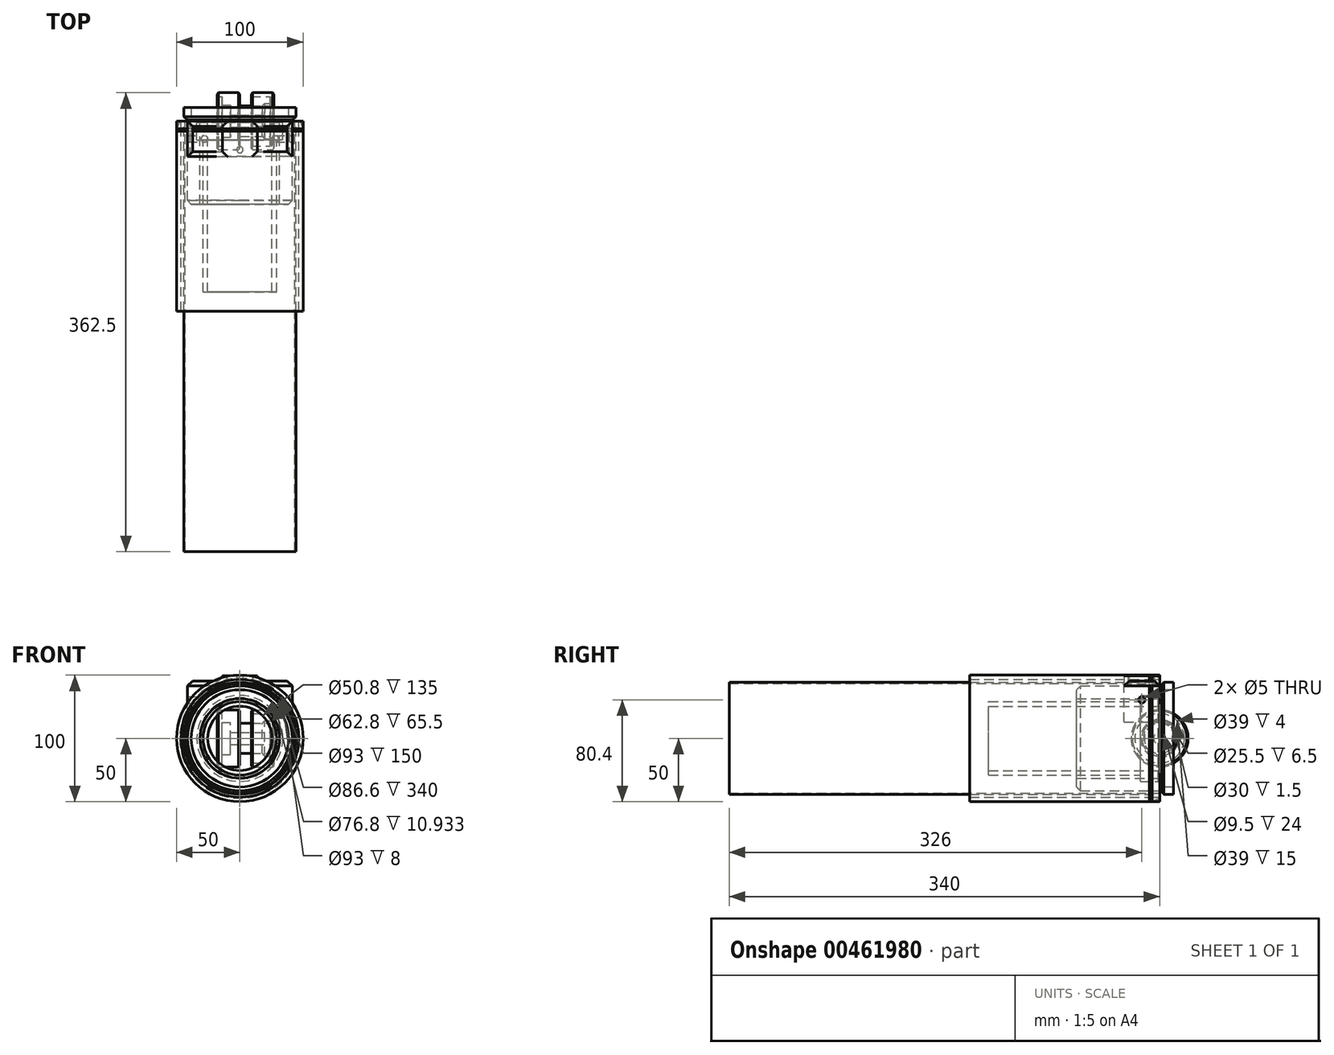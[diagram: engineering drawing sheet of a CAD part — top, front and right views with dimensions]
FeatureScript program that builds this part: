
annotation { "Feature Type Name" : "Feature", "Feature Type Description" : "" }
export const myFeature = defineFeature(function(context is Context, id is Id, definition is map)
    precondition{}
    {
        {
            var Q0;
            Q0=qCreatedBy(makeId("Front.planeOp"),FACE);
            var sketch = newSketch(context, id + "F0", { "sketchPlane" : qUnion([Q0])});
            skCircle(sketch, "E0", {"center": v(0, 0) * mm, "radius": 41.4 * mm});
            skCircle(sketch, "E1", {"center": v(0, 0) * mm, "radius": 31.4 * mm});
            skSolve(sketch);
        }
        {
            var Q0;
            Q0=makeQuery(id+"F0.imprint","IMPRINT",FACE,{"disambiguationData":[TD([[makeQuery(id+"F0.imprint","IMPRINT",EDGE,{"derivedFrom":sQuery(id+"F0.wireOp",EDGE,"E0")}),1.0]])]});
            extrude(context, id + "F1", {"entities" : qUnion([Q0]), "depth" : 65.5 * mm});
        }
        {
            var Q0;
            Q0=makeQuery(id+"F1.opExtrude","CAP_EDGE",EDGE,{"disambiguationData":[OSD([sQuery(id+"F0.wireOp",EDGE,"E0")])],"isStart":false});
            chamfer(context, id + "F2", {"entities" : qUnion([Q0]), "width" : 3 * mm, "tangentPropagation" : true});
        }
        {
            var Q0;
            Q0=qCreatedBy(makeId("Front.planeOp"),FACE);
            var sketch = newSketch(context, id + "F3", { "sketchPlane" : qUnion([Q0])});
            skCircle(sketch, "E2", {"center": v(0, 0) * mm, "radius": 25.4 * mm});
            skCircle(sketch, "E3", {"center": v(0, 0) * mm, "radius": 34 * mm});
            skSolve(sketch);
        }
        {
            var Q0;
            Q0=makeQuery(id+"F3.imprint","IMPRINT",FACE,{"disambiguationData":[TD([[makeQuery(id+"F3.imprint","IMPRINT",EDGE,{"derivedFrom":sQuery(id+"F3.wireOp",EDGE,"E2")}),-1.0]])]});
            extrude(context, id + "F4", {"entities" : qUnion([Q0]), "depth" : 15 * mm});
        }
        {
            var Q0;
            Q0=makeQuery(id+"F4.opExtrude","CAP_FACE",FACE,{"disambiguationData":[OSD([sQuery(id+"F3.wireOp",EDGE,"E2"),sQuery(id+"F3.wireOp",EDGE,"E3")])],"isStart":false});
            var sketch = newSketch(context, id + "F5", { "sketchPlane" : qUnion([Q0])});
            skCircle(sketch, "E4", {"center": v(0, 0) * mm, "radius": 29 * mm});
            skCircle(sketch, "E5", {"center": v(0, 0) * mm, "radius": 25.4 * mm});
            skSolve(sketch);
        }
        {
            var Q0;
            Q0=makeQuery(id+"F5.imprint","IMPRINT",FACE,{"disambiguationData":[TD([[makeQuery(id+"F5.imprint","IMPRINT",EDGE,{"derivedFrom":sQuery(id+"F5.wireOp",EDGE,"E4")}),1.0]])]});
            extrude(context, id + "F6", {"entities" : qUnion([Q0]), "operationType" : NewBodyOperationType.ADD, "depth" : 120 * mm});
        }
        {
            var Q0;
            Q0=makeQuery(id+"F4.opExtrude","CAP_EDGE",EDGE,{"disambiguationData":[OSD([sQuery(id+"F3.wireOp",EDGE,"E3")])],"isStart":true});
            chamfer(context, id + "F7", {"entities" : qUnion([Q0]), "chamferType" : ChamferType.TWO_OFFSETS, "width1" : 1 * mm, "oppositeDirection" : false, "width2" : 2 * mm, "tangentPropagation" : true});
        }
        {
            var Q0;
            Q0=qCreatedBy(makeId("Right.planeOp"),FACE);
            var sketch = newSketch(context, id + "F8", { "sketchPlane" : qUnion([Q0])});
            skLineSegment(sketch, "E6", {"start": v(0, 38.4) * mm, "end": v(10.93, 38.4) * mm});
            skLineSegment(sketch, "E7", {"start": v(10.93, 38.4) * mm, "end": v(10.93, 44.3) * mm});
            skLineSegment(sketch, "E8", {"start": v(10.93, 44.3) * mm, "end": v(3.43, 44.3) * mm});
            skLineSegment(sketch, "E9", {"start": v(3.43, 44.3) * mm, "end": v(1, 41.4) * mm});
            skLineSegment(sketch, "E10", {"start": v(1, 41.4) * mm, "end": v(0, 41.4) * mm});
            skLineSegment(sketch, "E11", {"start": v(0, 41.4) * mm, "end": v(0, 38.4) * mm});
            skLineSegment(sketch, "E12", {"start": v(0, 0) * mm, "end": v(10.93, 0) * mm, "construction": true});
            skSolve(sketch);
        }
        {
            var Q0;
            Q0=makeQuery(id+"F8.imprint","IMPRINT",FACE,{"disambiguationData":[TD([[makeQuery(id+"F8.imprint","IMPRINT",EDGE,{"derivedFrom":sQuery(id+"F8.wireOp",EDGE,"E6")}),1.0]])]});
            var Q1;
            Q1=sQuery(id+"F8.wireOp",EDGE,"E12");
            revolve(context, id + "F9", {"entities" : qUnion([Q0]), "axis" : qUnion([Q1]), "revolveType" : RevolveType.FULL});
        }
        {
            var Q0;
            Q0=qCreatedBy(makeId("Front.planeOp"),FACE);
            var sketch = newSketch(context, id + "F10", { "sketchPlane" : qUnion([Q0])});
            skLineSegment(sketch, "E13", {"start": v(-41.4, 13) * mm, "end": v(-41.4, 45.4) * mm});
            skLineSegment(sketch, "E14", {"start": v(-41.4, 45.4) * mm, "end": v(-13.75, 45.4) * mm});
            skLineSegment(sketch, "E15", {"start": v(-13.75, 45.4) * mm, "end": v(-13.75, 49.4) * mm});
            skLineSegment(sketch, "E16", {"start": v(-13.75, 49.4) * mm, "end": v(13.75, 49.4) * mm});
            skLineSegment(sketch, "E17", {"start": v(13.75, 49.4) * mm, "end": v(13.75, 45.4) * mm});
            skLineSegment(sketch, "E18", {"start": v(13.75, 45.4) * mm, "end": v(41.4, 45.4) * mm});
            skLineSegment(sketch, "E19", {"start": v(41.4, 45.4) * mm, "end": v(41.4, 13) * mm});
            skLineSegment(sketch, "E20", {"start": v(41.4, 13) * mm, "end": v(39.3, 13) * mm});
            skLineSegment(sketch, "E21", {"start": v(-41.4, 13) * mm, "end": v(-39.3, 13) * mm});
            skArc(sketch, "E22", {"start": v(-39.3, 13) * mm, "mid": v(0, 41.4) * mm, "end": v(39.3, 13) * mm});
            skSolve(sketch);
        }
        {
            var Q0;
            Q0=makeQuery(id+"F10.imprint","IMPRINT",FACE,{"disambiguationData":[TD([[makeQuery(id+"F10.imprint","IMPRINT",EDGE,{"derivedFrom":sQuery(id+"F10.wireOp",EDGE,"E13")}),-1.0]])]});
            extrude(context, id + "F11", {"entities" : qUnion([Q0]), "depth" : 28 * mm});
        }
        {
            var Q0;
            Q0=makeQuery(id+"F11.opExtrude","SWEPT_FACE",FACE,{"disambiguationData":[OSD([sQuery(id+"F10.wireOp",EDGE,"E16")])]});
            var sketch = newSketch(context, id + "F12", { "sketchPlane" : qUnion([Q0])});
            skPoint(sketch, "E23", {"position": v(0, -22.5) * mm});
            skSolve(sketch);
        }
        {
            var Q0;
            Q0=sQuery(id+"F12.wireOp",VERTEX,"E23");
            var Q1;
            Q1=makeQuery(id+"F11.opExtrude","SWEPT_BODY",BODY,{"disambiguationData":[OSD([sQuery(id+"F10.wireOp",EDGE,"E13"),sQuery(id+"F10.wireOp",EDGE,"E14"),sQuery(id+"F10.wireOp",EDGE,"E15"),sQuery(id+"F10.wireOp",EDGE,"E16"),sQuery(id+"F10.wireOp",EDGE,"E17"),sQuery(id+"F10.wireOp",EDGE,"E18"),sQuery(id+"F10.wireOp",EDGE,"E19"),sQuery(id+"F10.wireOp",EDGE,"E20"),sQuery(id+"F10.wireOp",EDGE,"E21"),sQuery(id+"F10.wireOp",EDGE,"E22")])]});
            hole(context, id + "F13", {"style" : HoleStyle.SIMPLE, "endStyle" : HoleEndStyle.THROUGH, "holeDiameter" : 5 * mm, "tappedDepth" : 12 * mm, "tapClearance" : 3, "locations" : qUnion([Q0]), "scope" : qUnion([Q1])});
        }
        {
            var Q0;
            Q0=makeQuery(id+"F11.opExtrude","SWEPT_EDGE",EDGE,{"disambiguationData":[OSD([sQuery(id+"F10.wireOp",EDGE,"E17"),sQuery(id+"F10.wireOp",EDGE,"E18")])]});
            var Q1;
            Q1=makeQuery(id+"F11.opExtrude","SWEPT_EDGE",EDGE,{"disambiguationData":[OSD([sQuery(id+"F10.wireOp",EDGE,"E14"),sQuery(id+"F10.wireOp",EDGE,"E15")])]});
            fillet(context, id + "F14", {"entities" : qUnion([Q0, Q1]), "radius" : 5 * mm, "tangentPropagation" : true, "allowEdgeOverflow" : false});
        }
        {
            var Q0;
            Q0=makeQuery(id+"F11.opExtrude","CAP_EDGE",EDGE,{"disambiguationData":[OSD([sQuery(id+"F10.wireOp",EDGE,"E14")])],"isStart":false});
            var Q1;
            Q1=makeQuery(id+"F11.opExtrude","SWEPT_EDGE",EDGE,{"disambiguationData":[OSD([sQuery(id+"F10.wireOp",EDGE,"E13"),sQuery(id+"F10.wireOp",EDGE,"E14")])]});
            var Q2;
            Q2=makeQuery(id+"F11.opExtrude","CAP_EDGE",EDGE,{"disambiguationData":[OSD([sQuery(id+"F10.wireOp",EDGE,"E14")])],"isStart":true});
            var Q3;
            Q3=makeQuery(id+"F11.opExtrude","CAP_EDGE",EDGE,{"disambiguationData":[OSD([sQuery(id+"F10.wireOp",EDGE,"E18")])],"isStart":true});
            var Q4;
            Q4=makeQuery(id+"F11.opExtrude","SWEPT_EDGE",EDGE,{"disambiguationData":[OSD([sQuery(id+"F10.wireOp",EDGE,"E18"),sQuery(id+"F10.wireOp",EDGE,"E19")])]});
            var Q5;
            Q5=makeQuery(id+"F11.opExtrude","CAP_EDGE",EDGE,{"disambiguationData":[OSD([sQuery(id+"F10.wireOp",EDGE,"E18")])],"isStart":false});
            chamfer(context, id + "F15", {"entities" : qUnion([Q0, Q1, Q2, Q3, Q4, Q5]), "width" : 4 * mm, "tangentPropagation" : true});
        }
        {
            var Q0;
            Q0=qCreatedBy(makeId("Front.planeOp"),FACE);
            var sketch = newSketch(context, id + "F16", { "sketchPlane" : qUnion([Q0])});
            skLineSegment(sketch, "E24", {"start": v(0, 12) * mm, "end": v(17.82, 12) * mm});
            skLineSegment(sketch, "E25", {"start": v(17.82, 12) * mm, "end": v(19.5, 14) * mm});
            skLineSegment(sketch, "E26", {"start": v(19.5, 14) * mm, "end": v(27, 14) * mm});
            skLineSegment(sketch, "E27", {"start": v(27, 14) * mm, "end": v(27, 0) * mm});
            skLineSegment(sketch, "E28", {"start": v(27, 0) * mm, "end": v(0, 0) * mm});
            skLineSegment(sketch, "E29", {"start": v(0, 0) * mm, "end": v(0, 12) * mm});
            skSolve(sketch);
        }
        {
            var Q0;
            Q0=makeQuery(id+"F16.imprint","IMPRINT",FACE,{"disambiguationData":[TD([[makeQuery(id+"F16.imprint","IMPRINT",EDGE,{"derivedFrom":sQuery(id+"F16.wireOp",EDGE,"E24")}),-1.0]])]});
            var Q1;
            Q1=sQuery(id+"F16.wireOp",EDGE,"E28");
            revolve(context, id + "F17", {"entities" : qUnion([Q0]), "axis" : qUnion([Q1]), "revolveType" : RevolveType.FULL});
        }
        {
            var Q0;
            Q0=makeQuery(id+"F11.opExtrude","SWEPT_FACE",FACE,{"disambiguationData":[OSD([sQuery(id+"F10.wireOp",EDGE,"E13")])]});
            var sketch = newSketch(context, id + "F18", { "sketchPlane" : qUnion([Q0])});
            skPoint(sketch, "E30", {"position": v(14, 30.4) * mm});
            skPoint(sketch, "E31", {"position": v(14, 13) * mm});
            skSolve(sketch);
        }
        {
            var Q0;
            Q0=sQuery(id+"F18.wireOp",VERTEX,"E30");
            var Q1;
            Q1=makeQuery(id+"F11.opExtrude","SWEPT_BODY",BODY,{"disambiguationData":[OSD([sQuery(id+"F10.wireOp",EDGE,"E13"),sQuery(id+"F10.wireOp",EDGE,"E14"),sQuery(id+"F10.wireOp",EDGE,"E15"),sQuery(id+"F10.wireOp",EDGE,"E16"),sQuery(id+"F10.wireOp",EDGE,"E17"),sQuery(id+"F10.wireOp",EDGE,"E18"),sQuery(id+"F10.wireOp",EDGE,"E19"),sQuery(id+"F10.wireOp",EDGE,"E20"),sQuery(id+"F10.wireOp",EDGE,"E21"),sQuery(id+"F10.wireOp",EDGE,"E22")])]});
            hole(context, id + "F19", {"style" : HoleStyle.SIMPLE, "endStyle" : HoleEndStyle.THROUGH, "holeDiameter" : 5 * mm, "tappedDepth" : 12 * mm, "tapClearance" : 3, "locations" : qUnion([Q0]), "scope" : qUnion([Q1])});
        }
        {
            var Q0;
            Q0=qCreatedBy(makeId("Front.planeOp"),FACE);
            var sketch = newSketch(context, id + "F20", { "sketchPlane" : qUnion([Q0])});
            skLineSegment(sketch, "E32", {"start": v(0, 22.5) * mm, "end": v(0, 15) * mm});
            skLineSegment(sketch, "E33", {"start": v(0, 15) * mm, "end": v(-1.5, 15) * mm});
            skLineSegment(sketch, "E34", {"start": v(-1.5, 15) * mm, "end": v(-1.5, 4.75) * mm});
            skLineSegment(sketch, "E35", {"start": v(-1.5, 4.75) * mm, "end": v(-7.5, 4.75) * mm});
            skLineSegment(sketch, "E36", {"start": v(-7.5, 4.75) * mm, "end": v(-7.5, 12.75) * mm});
            skLineSegment(sketch, "E37", {"start": v(-7.5, 12.75) * mm, "end": v(-14, 12.75) * mm});
            skLineSegment(sketch, "E38", {"start": v(-14, 12.75) * mm, "end": v(-14, 19.5) * mm});
            skLineSegment(sketch, "E39", {"start": v(-14, 19.5) * mm, "end": v(-18, 19.5) * mm});
            skLineSegment(sketch, "E40", {"start": v(-18, 19.5) * mm, "end": v(-18, 22.5) * mm});
            skLineSegment(sketch, "E41", {"start": v(-18, 22.5) * mm, "end": v(0, 22.5) * mm});
            skLineSegment(sketch, "E42", {"start": v(0, 0) * mm, "end": v(-18, 0) * mm, "construction": true});
            skSolve(sketch);
        }
        {
            var Q0;
            Q0=makeQuery(id+"F20.imprint","IMPRINT",FACE,{"disambiguationData":[TD([[makeQuery(id+"F20.imprint","IMPRINT",EDGE,{"derivedFrom":sQuery(id+"F20.wireOp",EDGE,"E32")}),-1.0]])]});
            var Q1;
            Q1=sQuery(id+"F20.wireOp",EDGE,"E42");
            revolve(context, id + "F21", {"entities" : qUnion([Q0]), "axis" : qUnion([Q1]), "revolveType" : RevolveType.FULL});
        }
        {
            var Q0;
            Q0=makeQuery(id+"F21.opRevolve","SWEPT_EDGE",EDGE,{"disambiguationData":[OSD([sQuery(id+"F20.wireOp",EDGE,"E32"),sQuery(id+"F20.wireOp",EDGE,"E41")])]});
            var Q1;
            Q1=makeQuery(id+"F21.opRevolve","SWEPT_EDGE",EDGE,{"disambiguationData":[OSD([sQuery(id+"F20.wireOp",EDGE,"E40"),sQuery(id+"F20.wireOp",EDGE,"E41")])]});
            chamfer(context, id + "F22", {"entities" : qUnion([Q0, Q1]), "width" : 1 * mm, "tangentPropagation" : true});
        }
        {
            var Q0;
            Q0=qCreatedBy(makeId("Front.planeOp"),FACE);
            var sketch = newSketch(context, id + "F23", { "sketchPlane" : qUnion([Q0])});
            skLineSegment(sketch, "E43", {"start": v(0, 4.75) * mm, "end": v(0, 12) * mm});
            skLineSegment(sketch, "E44", {"start": v(0, 12) * mm, "end": v(24, 12) * mm});
            skLineSegment(sketch, "E45", {"start": v(24, 12) * mm, "end": v(24, 19.5) * mm});
            skLineSegment(sketch, "E46", {"start": v(24, 19.5) * mm, "end": v(9, 19.5) * mm});
            skLineSegment(sketch, "E47", {"start": v(9, 19.5) * mm, "end": v(9, 22.5) * mm});
            skLineSegment(sketch, "E48", {"start": v(9, 22.5) * mm, "end": v(27, 22.5) * mm});
            skLineSegment(sketch, "E49", {"start": v(27, 22.5) * mm, "end": v(27, 0) * mm});
            skLineSegment(sketch, "E50", {"start": v(27, 0) * mm, "end": v(24, 0) * mm});
            skLineSegment(sketch, "E51", {"start": v(24, 0) * mm, "end": v(24, 4.75) * mm});
            skLineSegment(sketch, "E52", {"start": v(24, 4.75) * mm, "end": v(0, 4.75) * mm});
            skSolve(sketch);
        }
        {
            var Q0;
            Q0=makeQuery(id+"F23.imprint","IMPRINT",FACE,{"disambiguationData":[TD([[makeQuery(id+"F23.imprint","IMPRINT",EDGE,{"derivedFrom":sQuery(id+"F23.wireOp",EDGE,"E43")}),-1.0]])]});
            var Q1;
            Q1=sQuery(id+"F23.wireOp",EDGE,"E50");
            revolve(context, id + "F24", {"entities" : qUnion([Q0]), "axis" : qUnion([Q1]), "revolveType" : RevolveType.FULL});
        }
        {
            var Q0;
            Q0=makeQuery(id+"F24.opRevolve","SWEPT_EDGE",EDGE,{"disambiguationData":[OSD([sQuery(id+"F23.wireOp",EDGE,"E48"),sQuery(id+"F23.wireOp",EDGE,"E49")])]});
            var Q1;
            Q1=makeQuery(id+"F24.opRevolve","SWEPT_EDGE",EDGE,{"disambiguationData":[OSD([sQuery(id+"F23.wireOp",EDGE,"E47"),sQuery(id+"F23.wireOp",EDGE,"E48")])]});
            chamfer(context, id + "F25", {"entities" : qUnion([Q0, Q1]), "width" : 1 * mm, "tangentPropagation" : true});
        }
        {
            var Q0;
            Q0=qCreatedBy(makeId("Front.planeOp"),FACE);
            var sketch = newSketch(context, id + "F26", { "sketchPlane" : qUnion([Q0])});
            skCircle(sketch, "E53", {"center": v(0, 0) * mm, "radius": 44.3 * mm});
            skCircle(sketch, "E54", {"center": v(0, 0) * mm, "radius": 43.3 * mm});
            skSolve(sketch);
        }
        {
            var Q0;
            Q0 = qSketchRegion(id + "F26", true);
            extrude(context, id + "F27", {"entities" : qUnion([Q0]), "depth" : 340 * mm});
        }
        {
            var Q0;
            Q0=qCreatedBy(makeId("Front.planeOp"),FACE);
            var sketch = newSketch(context, id + "F28", { "sketchPlane" : qUnion([Q0])});
            skCircle(sketch, "E55", {"center": v(0, 0) * mm, "radius": 50 * mm});
            skCircle(sketch, "E56", {"center": v(0, 0) * mm, "radius": 46.5 * mm});
            skSolve(sketch);
        }
        {
            var Q0;
            Q0 = qSketchRegion(id + "F28", true);
            extrude(context, id + "F29", {"entities" : qUnion([Q0]), "depth" : 150 * mm});
        }
        {
            var Q0;
            Q0=qCreatedBy(makeId("Front.planeOp"),FACE);
            var sketch = newSketch(context, id + "F30", { "sketchPlane" : qUnion([Q0])});
            skCircle(sketch, "E57", {"center": v(0, 0) * mm, "radius": 50 * mm});
            skCircle(sketch, "E58", {"center": v(0, 0) * mm, "radius": 46.5 * mm});
            skSolve(sketch);
        }
        {
            var Q0;
            Q0=makeQuery(id+"F30.imprint","IMPRINT",FACE,{"disambiguationData":[TD([[makeQuery(id+"F30.imprint","IMPRINT",EDGE,{"derivedFrom":sQuery(id+"F30.wireOp",EDGE,"E57")}),1.0]])]});
            extrude(context, id + "F31", {"entities" : qUnion([Q0]), "depth" : 8 * mm});
        }
        {
            var Q0;
            Q0=makeQuery(id+"F31.opExtrude","CAP_EDGE",EDGE,{"disambiguationData":[OSD([sQuery(id+"F30.wireOp",EDGE,"E57")])],"isStart":true});
            chamfer(context, id + "F32", {"entities" : qUnion([Q0]), "chamferType" : ChamferType.TWO_OFFSETS, "width1" : 6 * mm, "oppositeDirection" : false, "width2" : 2.5 * mm, "tangentPropagation" : true});
        }
    });
